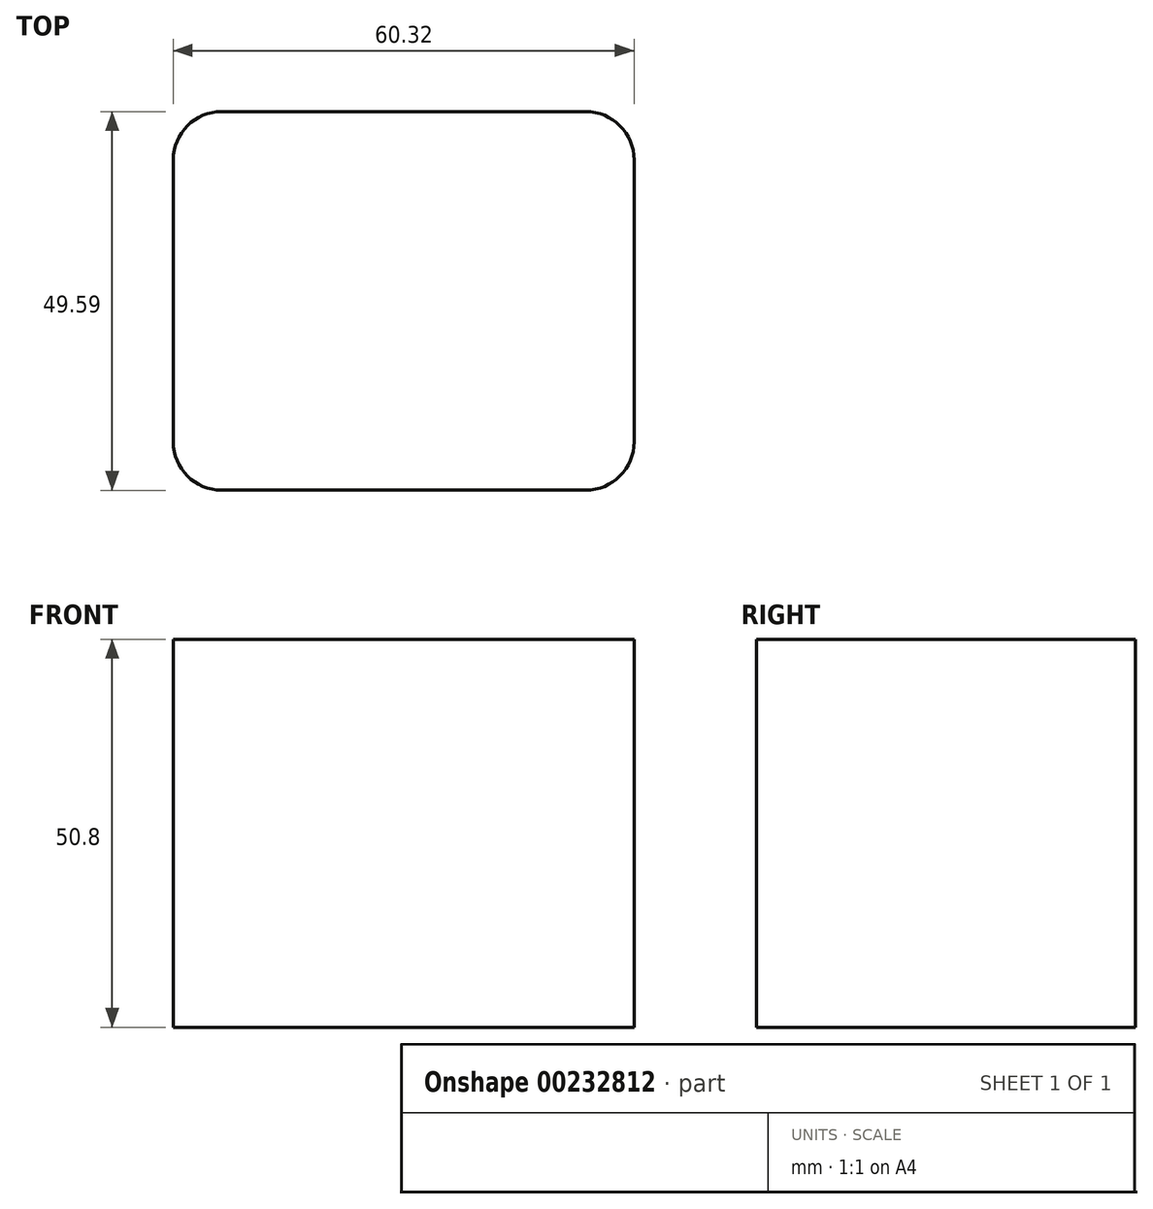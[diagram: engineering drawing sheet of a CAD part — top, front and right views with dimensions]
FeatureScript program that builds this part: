
annotation { "Feature Type Name" : "Feature", "Feature Type Description" : "" }
export const myFeature = defineFeature(function(context is Context, id is Id, definition is map)
    precondition{}
    {
        {
            var Q0;
            Q0=qCreatedBy(makeId("Top.planeOp"),FACE);
            var sketch = newSketch(context, id + "F0", { "sketchPlane" : qUnion([Q0])});
            skLineSegment(sketch, "E0.bottom", {"start": v(-12.05, -21.73) * mm, "end": v(35.57, -21.73) * mm});
            skLineSegment(sketch, "E0.top", {"start": v(-12.05, 27.86) * mm, "end": v(35.57, 27.86) * mm});
            skLineSegment(sketch, "E0.left", {"start": v(-18.4, -15.38) * mm, "end": v(-18.4, 21.51) * mm});
            skLineSegment(sketch, "E0.right", {"start": v(41.92, -15.38) * mm, "end": v(41.92, 21.51) * mm});
            skPoint(sketch, "E1.visualSharp", {"position": v(-18.4, 27.86) * mm});
            skArc(sketch, "E1.filletArc", {"start": v(-12.05, 27.86) * mm, "mid": v(-16.54, 26) * mm, "end": v(-18.4, 21.51) * mm});
            skPoint(sketch, "E2.visualSharp", {"position": v(41.92, 27.86) * mm});
            skArc(sketch, "E2.filletArc", {"start": v(41.92, 21.51) * mm, "mid": v(40.06, 26) * mm, "end": v(35.57, 27.86) * mm});
            skPoint(sketch, "E3.visualSharp", {"position": v(41.92, -21.73) * mm});
            skArc(sketch, "E3.filletArc", {"start": v(35.57, -21.73) * mm, "mid": v(40.06, -19.87) * mm, "end": v(41.92, -15.38) * mm});
            skPoint(sketch, "E4.visualSharp", {"position": v(-18.4, -21.73) * mm});
            skArc(sketch, "E4.filletArc", {"start": v(-18.4, -15.38) * mm, "mid": v(-16.54, -19.87) * mm, "end": v(-12.05, -21.73) * mm});
            skSolve(sketch);
        }
        {
            var Q0;
            Q0=makeQuery(id+"F0.imprint","IMPRINT",FACE,{"disambiguationData":[TD([[makeQuery(id+"F0.imprint","IMPRINT",EDGE,{"derivedFrom":sQuery(id+"F0.wireOp",EDGE,"E0.bottom")}),1.0]])]});
            extrude(context, id + "F1", {"entities" : qUnion([Q0]), "depth" : 50.8 * mm});
        }
    });
